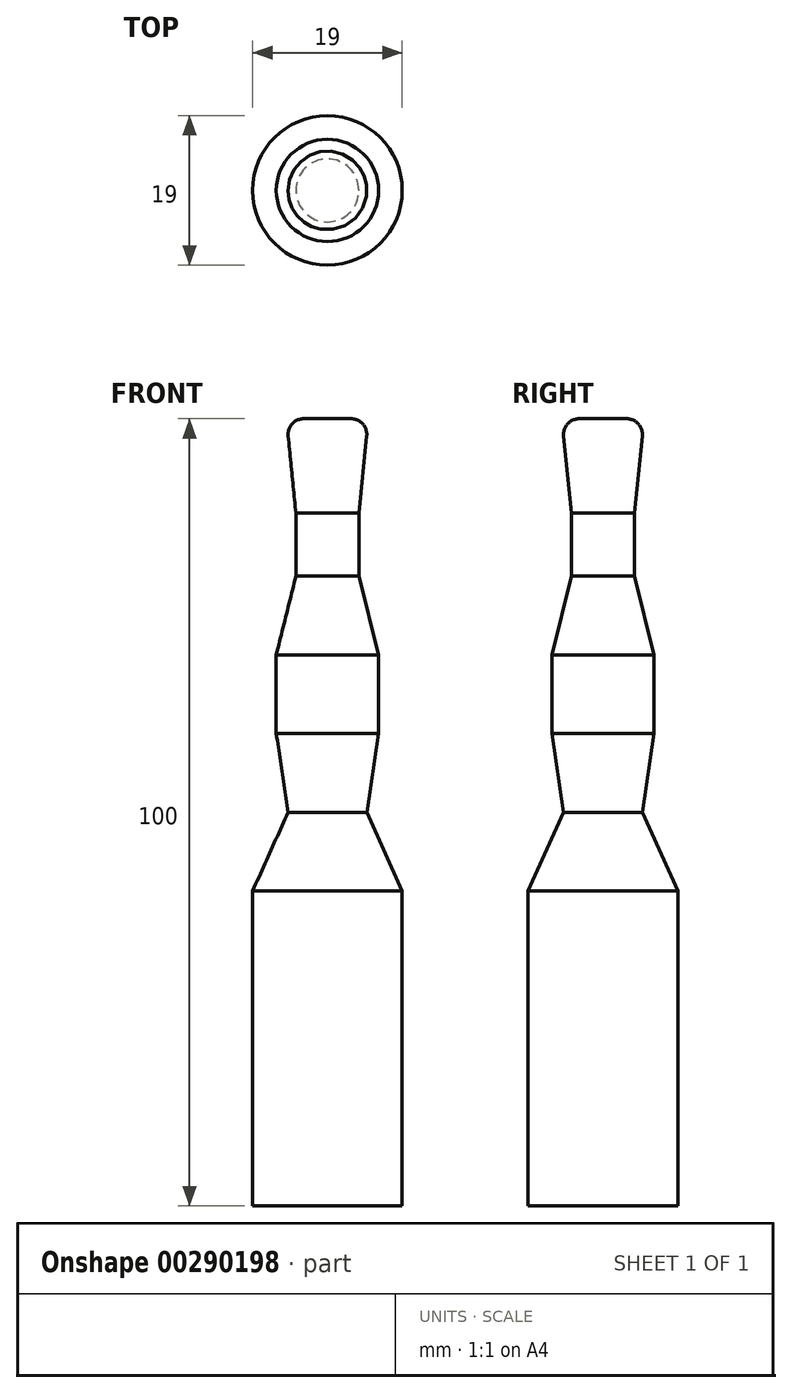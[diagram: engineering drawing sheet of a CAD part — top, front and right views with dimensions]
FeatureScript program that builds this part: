
annotation { "Feature Type Name" : "Feature", "Feature Type Description" : "" }
export const myFeature = defineFeature(function(context is Context, id is Id, definition is map)
    precondition{}
    {
        {
            var Q0;
            Q0=qCreatedBy(makeId("Front.planeOp"),FACE);
            var sketch = newSketch(context, id + "F0", { "sketchPlane" : qUnion([Q0])});
            skLineSegment(sketch, "E0", {"start": v(0, 0) * mm, "end": v(3, 0) * mm});
            skArc(sketch, "E1", {"start": v(4.99, -2.2) * mm, "mid": v(4.48, -0.66) * mm, "end": v(3, 0) * mm});
            skLineSegment(sketch, "E2", {"start": v(4.99, -2.2) * mm, "end": v(4, -12) * mm});
            skLineSegment(sketch, "E3", {"start": v(4, -12) * mm, "end": v(4, -20) * mm});
            skLineSegment(sketch, "E4", {"start": v(4, -20) * mm, "end": v(6.5, -30) * mm});
            skLineSegment(sketch, "E5", {"start": v(6.5, -30) * mm, "end": v(6.5, -40) * mm});
            skLineSegment(sketch, "E6", {"start": v(6.5, -40) * mm, "end": v(5, -50) * mm});
            skLineSegment(sketch, "E7", {"start": v(5, -50) * mm, "end": v(9.5, -60) * mm});
            skLineSegment(sketch, "E8", {"start": v(9.5, -60) * mm, "end": v(9.5, -100) * mm});
            skLineSegment(sketch, "E9", {"start": v(9.5, -100) * mm, "end": v(0, -100) * mm});
            skLineSegment(sketch, "E10", {"start": v(0, -100) * mm, "end": v(0, 0) * mm});
            skSolve(sketch);
        }
        {
            var Q0;
            Q0 = qSketchRegion(id + "F0", true);
            var Q1;
            Q1=sQuery(id+"F0.wireOp",EDGE,"E10");
            revolve(context, id + "F1", {"entities" : qUnion([Q0]), "axis" : qUnion([Q1]), "revolveType" : RevolveType.FULL});
        }
    });
